# Revit family: KEUCO_14983010037
name_source: partatom
category: Allgemeines Modell
revit_build: Autodesk Revit 2016 (Build: 20150220_1215(x64)
units: mm (PartAtom-declared; Revit-internal decimal feet)

## family parameters
Arbeitsebenenbasiert = Ja
Beim Laden mit Abzugskörper schneiden = Nein
Bemaßung runder Anschluss = Durchmesser verwenden
Gemeinsam genutzt = Nein
Immer vertikal = Nein
Kann Basisbauteil für Bewehrung sein = Nein
Raumberechnungspunkt = Nein
Teiletyp = Normal

## types (6) — shared parameters
Beschreibung = zur Wandmontage
Softsitz nach oben klappbar
Gewicht = 0.522
Hersteller = KEUCO
Kategorie = ACC
Länge = 370 mm  [stored 1.21391 ft]
Serie = Plan
Tiefe = 397 mm  [stored 1.30249 ft]
URL = https://www.keuco.com
Verwendung = DU
Vorgabe-Ansicht = 1219 mm

## per-type parameters (varying)
| type | Ausschreibungstext | Material Regal | Rahmen Material |
| 14983010037 | KEUCO PLAN Klappsitz 14983010037
Schwarzgrauer Klappsitz (RAL 7021) aus Polyurethan-Schaum 
in ästhetischem, funktionalem Design, zur Wandmontage
für sicheres Sitzen im Duschbereich
Wandhalter und Sitzträger als Design-Element hochglanzverchromt
antistatisch, leichte Reinigung 
kann mit max. 60%-igen Ethanol- oder Propanol-Lösungen desinfiziert werden, 
andere Desinfektionsmittel empfehlen sich nicht
nach oben klappbarer Softsitz, belastbar bis 150 kg
Breite 370 mm, Länge der Sitzfläche 360 mm
Ausladung 397 mm
Der Sitz wird verdeckt angebracht 
TÜVRheinland zertifiziert
Das Befestigungsmaterial ist separat zu bestellen!

Zur Montage (je nach Ankergrund/Mauerwerk) unbedingt erforderlich:

3 x Befestigungs-Set 3 (Artikel-Nr. 34992000100)
oder
3 x Befestigungs-Set 6 (Artikel-Nr. 34992000200)
oder
3 x Befestigungs-Set 9 (Artikel-Nr. 34995000200)
oder
3 x Befestigungs-Set 11 (Artikel-Nr. 34997000100) | Schwarzgrau (RAL 7021) | Verchromt |
| 14983010038 | KEUCO PLAN Klappsitz 14983010038
Lichtgrauer Klappsitz (RAL 7035) aus Polyurethan-Schaum 
in ästhetischem, funktionalem Design, zur Wandmontage
für sicheres Sitzen im Duschbereich
Wandhalter und Sitzträger als Design-Element hochglanzverchromt.
antistatisch, leichte Reinigung.
kann mit max. 60%-igen Ethanol- oder Propanol-Lösungen desinfiziert werden, 
andere Desinfektionsmittel empfehlen sich nicht
nach Oben klappbarer Softsitz, belastbar bis 150 kg
Breite 370 mm, Länge der Sitzfläche 360 mm
Ausladung 397 mm
Der Sitz wird verdeckt angebracht und ist 
Das Befestigungsmaterial ist separat zu bestellen!
TÜVRheinland zertifiziert
Zur Montage (je nach Ankergrund/Mauerwerk) unbedingt erforderlich:

1 x Befestigungs-Set 3 (Artikel-Nr. 34992000100)
oder
1 x Befestigungs-Set 6 (Artikel-Nr. 34992000200)
oder
1 x Befestigungs-Set 9 (Artikel-Nr. 34995000200)
oder
1 x Befestigungs-Set 11 (Artikel-Nr. 34997000100) | Lichtgrau (RAL 7035) | Verchromt |
| 14983010051 | KEUCO PLAN Klappsitz 14983010051
Weißer Klappsitz (RAL 9010) aus Polyurethan-Schaum 
in ästhetischem, funktionalem Design, zur Wandmontage
für sicheres Sitzen im Duschbereich
Wandhalter und Sitzträger als Design-Element hochglanzverchromt
antistatisch, leichte Reinigung 
kann mit max. 60%-igen Ethanol- oder Propanol-Lösungen desinfiziert werden, 
andere Desinfektionsmittel empfehlen sich nicht
nach oben klappbarer Softsitz, belastbar bis 150 kg
Breite 370 mm, Länge der Sitzfläche 360 mm
Ausladung 397 mm
Der Sitz wird verdeckt angebracht 
TÜVRheinland zertifiziert
Das Befestigungsmaterial ist separat zu bestellen!

Zur Montage (je nach Ankergrund/Mauerwerk) unbedingt erforderlich:

3 x Befestigungs-Set 3 (Artikel-Nr. 34992000100)
oder
3 x Befestigungs-Set 6 (Artikel-Nr. 34992000200)
oder
3 x Befestigungs-Set 9 (Artikel-Nr. 34995000200)
oder
3 x Befestigungs-Set 11 (Artikel-Nr. 34997000100) | Weiß (RAL 9010) | Verchromt |
| 14983170037 | KEUCO PLAN Klappsitz 14983170037
Schwarzgrauer Klappsitz (RAL 7021) aus Polyurethan-Schaum 
in ästhetischem, funktionalem Design, zur Wandmontage
für sicheres Sitzen im Duschbereich
Wandhalter und Sitzträger als Design-Element in lackiertem Aluminium.
antistatisch, leichte Reinigung 
kann mit max. 60%-igen Ethanol- oder Propanol-Lösungen desinfiziert werden, 
andere Desinfektionsmittel empfehlen sich nicht
nach oben klappbarer Softsitz, belastbar bis 150 kg
Breite 370 mm, Länge der Sitzfläche 360 mm
Ausladung 397 mm
Der Sitz wird verdeckt angebracht 
TÜVRheinland zertifiziert
Das Befestigungsmaterial ist separat zu bestellen!

Zur Montage (je nach Ankergrund/Mauerwerk) unbedingt erforderlich:

3 x Befestigungs-Set 3 (Artikel-Nr. 34992000100)
oder
3 x Befestigungs-Set 6 (Artikel-Nr. 34992000200)
oder
3 x Befestigungs-Set 9 (Artikel-Nr. 34995000200)
oder
3 x Befestigungs-Set 11 (Artikel-Nr. 34997000100) | Schwarzgrau (RAL 7021) | Aluminium silber-eloxiert (E6 EV1) |
| 14983170038 | KEUCO PLAN Klappsitz 14983170038
Lichtgrauer Klappsitz (RAL 7035) aus Polyurethan-Schaum 
in ästhetischem, funktionalem Design, zur Wandmontage
für sicheres Sitzen im Duschbereich
Wandhalter und Sitzträger als Design Element in lackiertem Aluminium
antistatisch, leichte Reinigung 
kann mit max. 60%-igen Ethanol- oder Propanol-Lösungen desinfiziert werden, 
andere Desinfektionsmittel empfehlen sich nicht
nach oben klappbarer Softsitz, belastbar bis 150 kg
Breite 370 mm, Länge der Sitzfläche 360 mm
Ausladung 397 mm
Der Sitz wird verdeckt angebracht 
TÜVRheinland zertifiziert
Das Befestigungsmaterial ist separat zu bestellen!

Zur Montage (je nach Ankergrund/Mauerwerk) unbedingt erforderlich:

3 x Befestigungs-Set 3 (Artikel-Nr. 34992000100)
oder
3 x Befestigungs-Set 6 (Artikel-Nr. 34992000200)
oder
3 x Befestigungs-Set 9 (Artikel-Nr. 34995000200)
oder
3 x Befestigungs-Set 11 (Artikel-Nr. 34997000100) | Lichtgrau (RAL 7035) | Verchromt |
| 14983170051 | KEUCO PLAN Klappsitz 14983170051
Weißer Klappsitz (RAL 6010) aus Polyurethan-Schaum 
in ästhetischem, funktionalem Design, zur Wandmontage
für sicheres Sitzen im Duschbereich
Wandhalter und Sitzträger als Design-Element in lackiertem Aluminium.
antistatisch, leichte Reinigung 
kann mit max. 60%-igen Ethanol- oder Propanol-Lösungen desinfiziert werden, 
andere Desinfektionsmittel empfehlen sich nicht
nach oben klappbarer Softsitz, belastbar bis 150 kg
Breite 370 mm, Länge der Sitzfläche 360 mm
Ausladung 397 mm
Der Sitz wird verdeckt angebracht
TÜVRheinland zertifiziert 
Das Befestigungsmaterial ist separat zu bestellen!

Zur Montage (je nach Ankergrund/Mauerwerk) unbedingt erforderlich:

3 x Befestigungs-Set 3 (Artikel-Nr. 34992000100)
oder
3 x Befestigungs-Set 6 (Artikel-Nr. 34992000200)
oder
3 x Befestigungs-Set 9 (Artikel-Nr. 34995000200)
oder
3 x Befestigungs-Set 11 (Artikel-Nr. 34997000100) | Weiß (RAL 9010) | Aluminium silber-eloxiert (E6 EV1) |

note: column(s) folded — value = type name in every type: Artikelnummer

note: [stored X ft] marks values corroborated as IEEE doubles in the binary element streams (Revit-internal decimal feet)

## geometry (parser evidence)
native form markers: Blend x2, Sweep x3
no freeform markers — native parametric forms only
